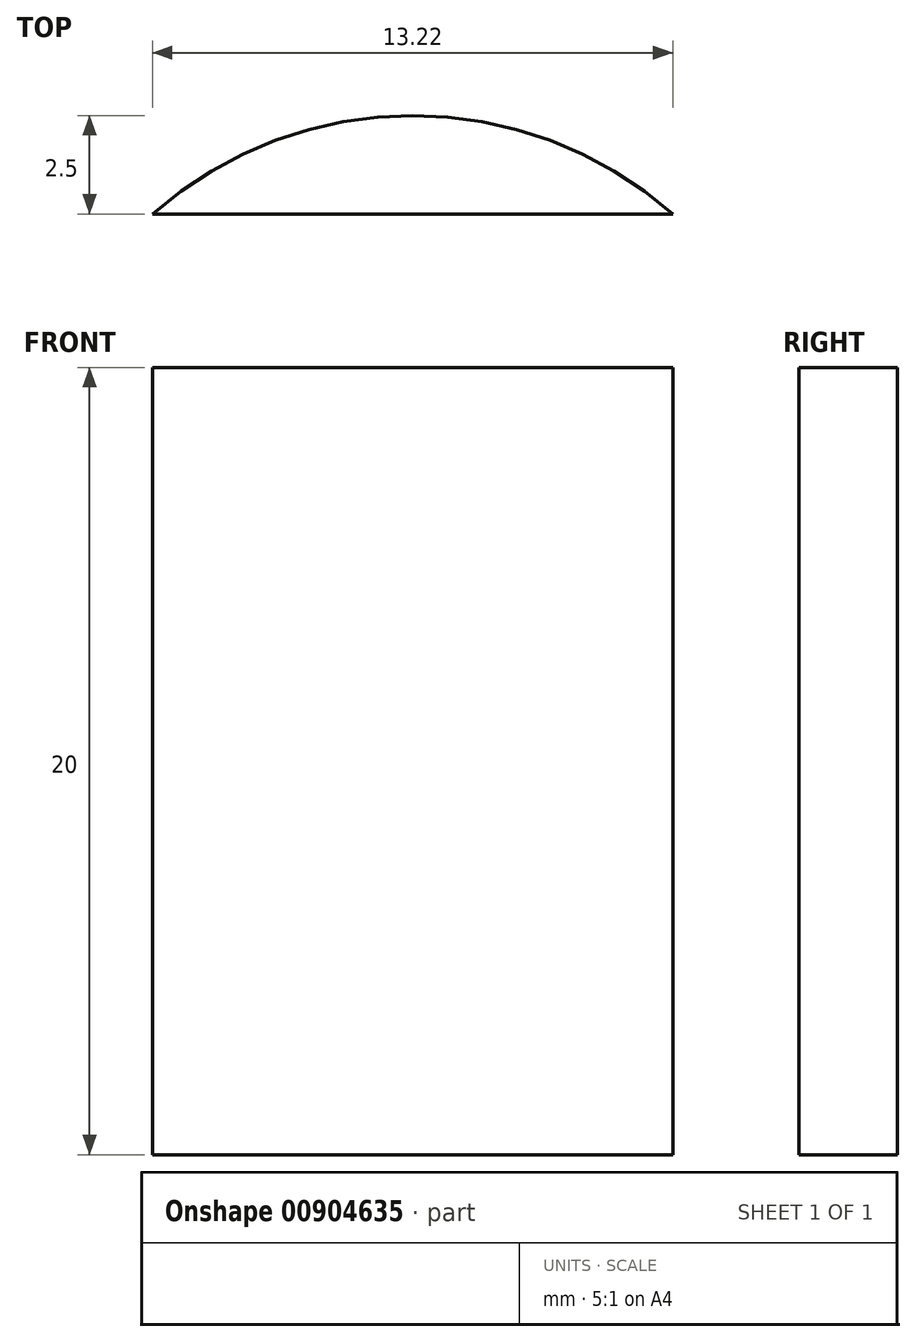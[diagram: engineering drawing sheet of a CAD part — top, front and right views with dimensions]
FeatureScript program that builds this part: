
annotation { "Feature Type Name" : "Feature", "Feature Type Description" : "" }
export const myFeature = defineFeature(function(context is Context, id is Id, definition is map)
    precondition{}
    {
        {
            var Q0;
            Q0=qCreatedBy(makeId("Top.planeOp"),FACE);
            var sketch = newSketch(context, id + "F0", { "sketchPlane" : qUnion([Q0])});
            skCircle(sketch, "E0", {"center": v(0, 0) * mm, "radius": 10 * mm});
            skLineSegment(sketch, "E1.bottom", {"start": v(-25.4, 7.5) * mm, "end": v(24.6, 7.5) * mm});
            skLineSegment(sketch, "E1.top", {"start": v(-25.4, -7.5) * mm, "end": v(24.6, -7.5) * mm});
            skLineSegment(sketch, "E1.left", {"start": v(-25.4, 7.5) * mm, "end": v(-25.4, -7.5) * mm});
            skLineSegment(sketch, "E1.right", {"start": v(24.6, 7.5) * mm, "end": v(24.6, -7.5) * mm});
            skSolve(sketch);
        }
        {
            var Q0;
            {var subQ0=sQuery(id+"F0.wireOp",EDGE,"E1.bottom");var subQ1=sQuery(id+"F0.wireOp",EDGE,"E0");var subQ2=makeQuery(id+"F0.imprint","INTERSECT",VERTEX,{"disambiguationData":[OD(0.0)],"derivedFrom":[subQ1,subQ0]});Q0=makeQuery(id+"F0.imprint","IMPRINT",FACE,{"disambiguationData":[TD([[makeQuery(id+"F0.imprint","IMPRINT",EDGE,{"disambiguationData":[TD([[subQ2,-1.0]])],"derivedFrom":subQ1}),1.0]])]});}
            extrude(context, id + "F1", {"entities" : qUnion([Q0]), "depth" : 20 * mm, "offsetDistance" : 25 * mm});
        }
    });
